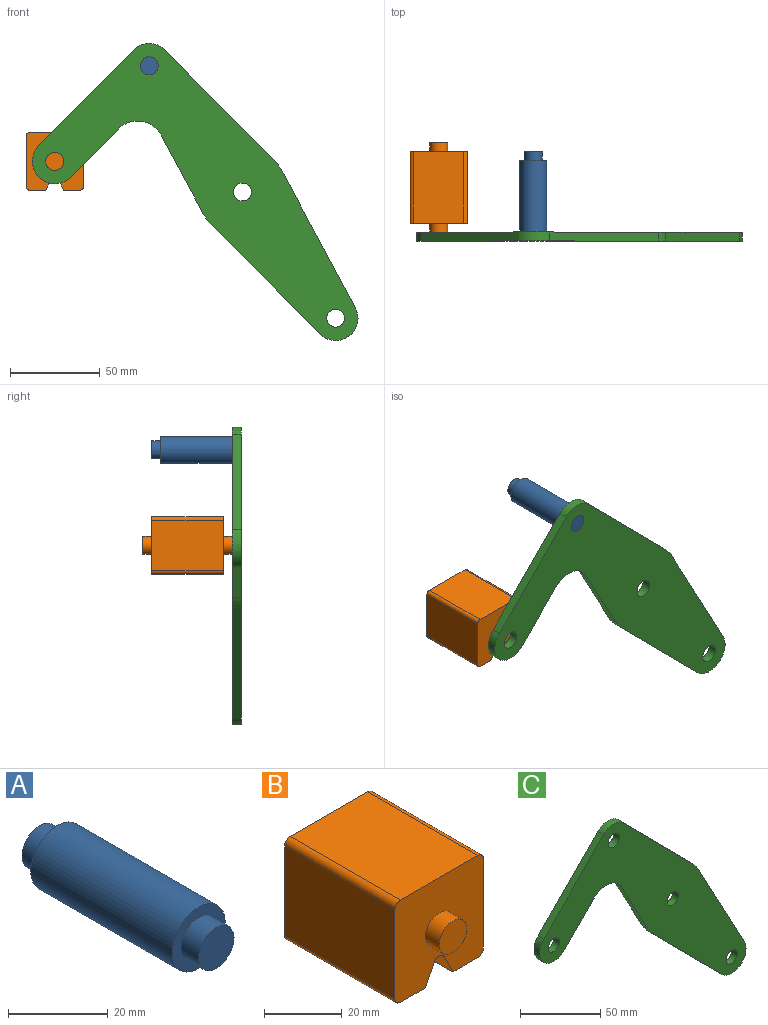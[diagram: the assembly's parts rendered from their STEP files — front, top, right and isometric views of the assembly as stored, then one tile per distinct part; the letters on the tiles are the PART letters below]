
ASSEMBLY  parts=3 mates=1
PART A: 7 faces, bbox 15x50x15 mm
  f0: cylinder r=7.5mm len=40mm, axis (0,-1,0), area 1885mm2, adj f2,f5
  f1: cylinder r=5mm len=10mm, axis (0,1,0), area 157.1mm2, adj f2,f3
  f2: plane 15x15mm, normal (0,-1,0), area 98.2mm2, adj f0,f1
  f3: plane 10x10mm, normal (0,-1,0), area 78.5mm2, adj f1
  f4: cylinder r=5mm len=10mm, axis (0,-1,0), area 157.1mm2, adj f5,f6
  f5: plane 15x15mm, normal (0,1,0), area 98.2mm2, adj f0,f4
  f6: plane 10x10mm, normal (0,1,0), area 78.5mm2, adj f4
PART B: 18 faces, bbox 32.1x50x32.1 mm
  f0: plane 40x28.08mm, normal (1,0,0), area 1123.1mm2, adj f4,f10,f13,f14
  f1: plane 40x9.04mm, normal (0,0,-1), area 361.6mm2, adj f2,f4,f10,f14
  f2: plane 40x6.42mm, normal (-0.89,0,-0.45), area 287.2mm2, adj f1,f4,f10,f15
  f3: plane 40x6.42mm, normal (0.89,0,-0.45), area 287.2mm2, adj f4,f5,f10,f15
  f4: plane 32.08x32.08mm, normal (0,-1,0), area 900.6mm2, adj f0,f1,f2,f3,f5,f6,f7,f9
  f5: plane 40x9.04mm, normal (0,0,-1), area 361.6mm2, adj f3,f4,f10,f16
  f6: plane 40x28.08mm, normal (0,0,1), area 1123.1mm2, adj f4,f10,f13,f17
  f7: plane 40x28.08mm, normal (-1,0,0), area 1123.1mm2, adj f4,f10,f16,f17
  f8: plane 10x10mm, normal (0,-1,0), area 78.5mm2, adj f9
  f9: cylinder r=5mm len=10mm, axis (0,1,0), area 157.1mm2, adj f4,f8
  f10: plane 32.08x32.08mm, normal (0,1,0), area 900.6mm2, adj f0,f1,f2,f3,f5,f6,f7,f12
  f11: plane 10x10mm, normal (0,1,0), area 78.5mm2, adj f12
  f12: cylinder r=5mm len=10mm, axis (0,-1,0), area 157.1mm2, adj f10,f11
  f13: cylinder r=2mm len=40mm, axis (0,1,0), area 125.7mm2, adj f0,f4,f6,f10
  f14: cylinder r=2mm len=40mm, axis (0,-1,0), area 125.7mm2, adj f0,f1,f4,f10
  f15: cylinder r=2mm len=40mm, axis (0,1,0), area 177.1mm2, adj f2,f3,f4,f10
  f16: cylinder r=2mm len=40mm, axis (0,1,0), area 125.7mm2, adj f4,f5,f7,f10
  f17: cylinder r=2mm len=40mm, axis (0,-1,0), area 125.7mm2, adj f4,f6,f7,f10
PART C: 18 faces, bbox 181.7x5x165.8 mm
  f0: plane 43.49x23.35mm, normal (-0.88,0,-0.47), area 246.8mm2, adj f1,f14,f16,f17
  f1: cylinder r=25mm len=5.75mm, axis (0,1,0), area 35.8mm2, adj f0,f2,f16,f17
  f2: plane 61.6x60.87mm, normal (-0.71,0,-0.7), area 433mm2, adj f1,f3,f16,f17
  f3: cylinder r=12.5mm len=21.39mm, axis (0,1,0), area 178.4mm2, adj f2,f4,f16,f17
  f4: plane 76.3x40.96mm, normal (0.88,0,0.47), area 433mm2, adj f3,f5,f16,f17
  f5: cylinder r=25mm len=5.75mm, axis (0,1,0), area 35.8mm2, adj f4,f6,f16,f17
  f6: plane 61.6x60.87mm, normal (0.71,0,0.7), area 433mm2, adj f5,f7,f16,f17
  f7: cylinder r=12.5mm len=17.78mm, axis (0,1,0), area 98.9mm2, adj f6,f8,f16,f17
  f8: plane 53.35x52.71mm, normal (-0.71,0,0.7), area 375mm2, adj f7,f9,f16,f17
  f9: cylinder r=12.5mm len=21.39mm, axis (0,1,0), area 196.3mm2, adj f8,f10,f16,f17
  f10: plane 26.86x26.54mm, normal (0.71,0,-0.7), area 188.8mm2, adj f9,f14,f16,f17
  f11: cylinder r=5mm len=10mm, axis (0,1,0), area 157.1mm2, adj f16,f17
  f12: cylinder r=5mm len=10mm, axis (0,1,0), area 157.1mm2, adj f16,f17
  f13: cylinder r=5mm len=10mm, axis (0,1,0), area 157.1mm2, adj f16,f17
  f14: cylinder r=15mm len=23.89mm, axis (0,1,0), area 140.2mm2, adj f0,f10,f16,f17
  f15: cylinder r=5mm len=10mm, axis (0,1,0), area 157.1mm2, adj f16,f17
  f16: plane 181.66x165.78mm, normal (0,-1,0), area 8710.1mm2, adj f0,f1,f2,f3,f4,f5,f6,f7
  f17: plane 181.66x165.78mm, normal (0,1,0), area 8710.1mm2, adj f0,f1,f2,f3,f4,f5,f6,f7
PLACE A t=(-6.18,-14.83,-4.32)mm
PLACE B t=(-6.18,-9.83,-4.32)mm
PLACE C t=(-6.18,-14.83,-4.32)mm
MATE revolute B.f9 <-> C.f9  axis (0,-1,0) through (-110.87,-14.83,12.72)mm
